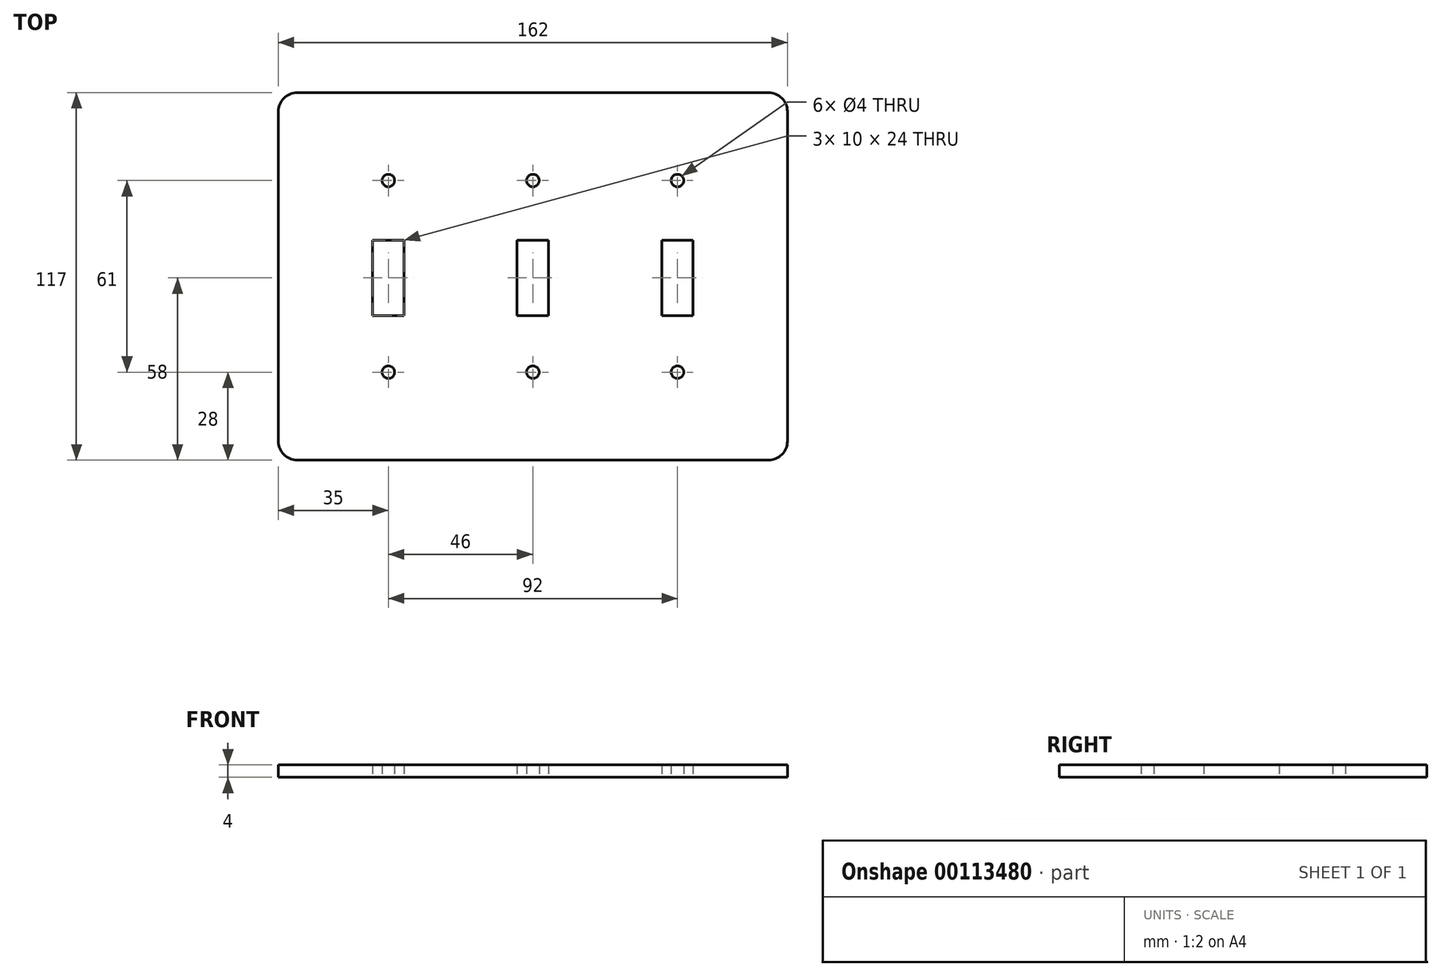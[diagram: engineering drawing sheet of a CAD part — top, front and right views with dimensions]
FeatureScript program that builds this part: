
annotation { "Feature Type Name" : "Feature", "Feature Type Description" : "" }
export const myFeature = defineFeature(function(context is Context, id is Id, definition is map)
    precondition{}
    {
        {
            var Q0;
            Q0=qCreatedBy(makeId("Top.planeOp"),FACE);
            var sketch = newSketch(context, id + "F0", { "sketchPlane" : qUnion([Q0])});
            skLineSegment(sketch, "E0.bottom", {"start": v(0, 0) * mm, "end": v(162, 0) * mm});
            skLineSegment(sketch, "E0.top", {"start": v(0, 117) * mm, "end": v(162, 117) * mm});
            skLineSegment(sketch, "E0.left", {"start": v(0, 0) * mm, "end": v(0, 117) * mm});
            skLineSegment(sketch, "E0.right", {"start": v(162, 0) * mm, "end": v(162, 117) * mm});
            skLineSegment(sketch, "E1.bottom", {"start": v(122, 70) * mm, "end": v(132, 70) * mm});
            skLineSegment(sketch, "E1.top", {"start": v(122, 46) * mm, "end": v(132, 46) * mm});
            skLineSegment(sketch, "E1.left", {"start": v(122, 70) * mm, "end": v(122, 46) * mm});
            skLineSegment(sketch, "E1.right", {"start": v(132, 70) * mm, "end": v(132, 46) * mm});
            skCircle(sketch, "E2", {"center": v(127, 89) * mm, "radius": 2 * mm});
            skCircle(sketch, "E3", {"center": v(127, 28) * mm, "radius": 2 * mm});
            skLineSegment(sketch, "E4.1.0.0", {"start": v(76, 70) * mm, "end": v(76, 46) * mm});
            skLineSegment(sketch, "E4.1.0.1", {"start": v(76, 46) * mm, "end": v(86, 46) * mm});
            skLineSegment(sketch, "E4.1.0.2", {"start": v(76, 70) * mm, "end": v(86, 70) * mm});
            skLineSegment(sketch, "E4.1.0.3", {"start": v(86, 70) * mm, "end": v(86, 46) * mm});
            skCircle(sketch, "E4.1.0.4", {"center": v(81, 89) * mm, "radius": 2 * mm});
            skCircle(sketch, "E4.1.0.5", {"center": v(81, 28) * mm, "radius": 2 * mm});
            skLineSegment(sketch, "E4.2.0.0", {"start": v(30, 70) * mm, "end": v(30, 46) * mm});
            skLineSegment(sketch, "E4.2.0.1", {"start": v(30, 46) * mm, "end": v(40, 46) * mm});
            skLineSegment(sketch, "E4.2.0.2", {"start": v(30, 70) * mm, "end": v(40, 70) * mm});
            skLineSegment(sketch, "E4.2.0.3", {"start": v(40, 70) * mm, "end": v(40, 46) * mm});
            skCircle(sketch, "E4.2.0.4", {"center": v(35, 89) * mm, "radius": 2 * mm});
            skCircle(sketch, "E4.2.0.5", {"center": v(35, 28) * mm, "radius": 2 * mm});
            skLineSegment(sketch, "E4.direction1", {"start": v(127, 28) * mm, "end": v(81, 28) * mm, "construction": true});
            skSolve(sketch);
        }
        {
            var Q0;
            Q0=qSketchRegion(id+"F0",true);
            extrude(context, id + "F1", {"entities" : qUnion([Q0]), "depth" : 4 * mm});
        }
        {
            var Q0;
            Q0=makeQuery(id+"F1.opExtrude","SWEPT_EDGE",EDGE,{"disambiguationData":[OSD([sQuery(id+"F0.wireOp",EDGE,"E0.top"),sQuery(id+"F0.wireOp",EDGE,"E0.left")])]});
            var Q1;
            Q1=makeQuery(id+"F1.opExtrude","SWEPT_EDGE",EDGE,{"disambiguationData":[OSD([sQuery(id+"F0.wireOp",EDGE,"E0.top"),sQuery(id+"F0.wireOp",EDGE,"E0.right")])]});
            var Q2;
            Q2=makeQuery(id+"F1.opExtrude","SWEPT_EDGE",EDGE,{"disambiguationData":[OSD([sQuery(id+"F0.wireOp",EDGE,"E0.bottom"),sQuery(id+"F0.wireOp",EDGE,"E0.right")])]});
            var Q3;
            Q3=makeQuery(id+"F1.opExtrude","SWEPT_EDGE",EDGE,{"disambiguationData":[OSD([sQuery(id+"F0.wireOp",EDGE,"E0.bottom"),sQuery(id+"F0.wireOp",EDGE,"E0.left")])]});
            fillet(context, id + "F2", {"entities" : qUnion([Q0, Q1, Q2, Q3]), "radius" : 6 * mm, "tangentPropagation" : true, "allowEdgeOverflow" : false});
        }
    });
